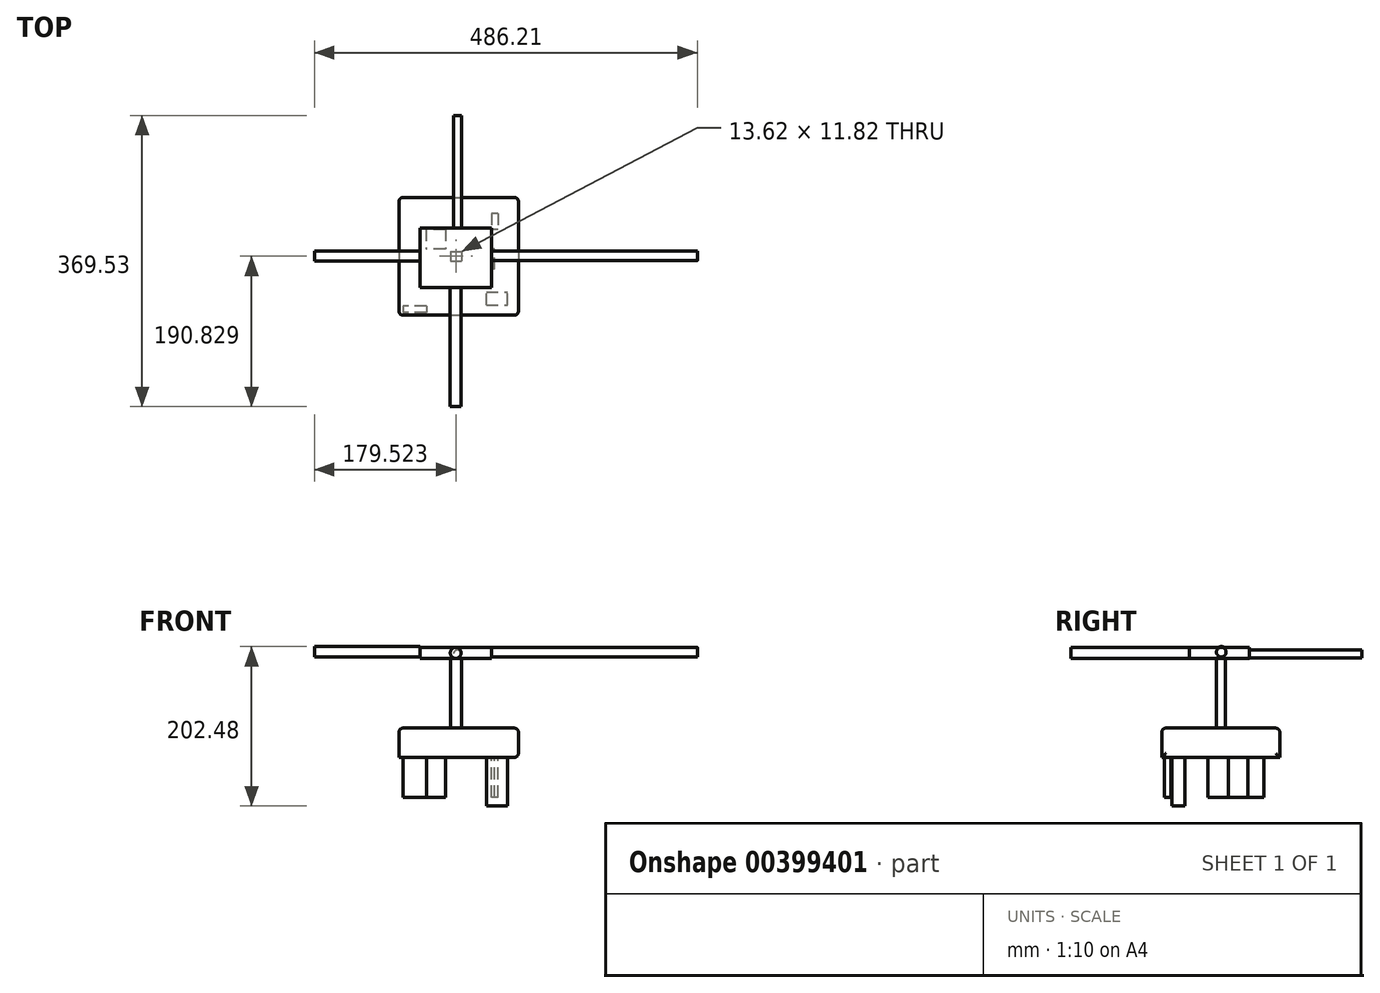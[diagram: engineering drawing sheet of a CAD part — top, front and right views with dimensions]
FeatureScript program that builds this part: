
annotation { "Feature Type Name" : "Feature", "Feature Type Description" : "" }
export const myFeature = defineFeature(function(context is Context, id is Id, definition is map)
    precondition{}
    {
        {
            var Q0;
            Q0=qCreatedBy(makeId("Top.planeOp"),FACE);
            var sketch = newSketch(context, id + "F0", { "sketchPlane" : qUnion([Q0])});
            skLineSegment(sketch, "E0.bottom", {"start": v(-74.23, 74.28) * mm, "end": v(77.35, 74.28) * mm});
            skLineSegment(sketch, "E0.top", {"start": v(-74.23, -75.35) * mm, "end": v(77.35, -75.35) * mm});
            skLineSegment(sketch, "E0.left", {"start": v(-74.23, 74.28) * mm, "end": v(-74.23, -75.35) * mm});
            skLineSegment(sketch, "E0.right", {"start": v(77.35, 74.28) * mm, "end": v(77.35, -75.35) * mm});
            skSolve(sketch);
        }
        {
            var Q0;
            Q0=makeQuery(id+"F0.imprint","IMPRINT",FACE,{"disambiguationData":[TD([[makeQuery(id+"F0.imprint","IMPRINT",EDGE,{"derivedFrom":sQuery(id+"F0.wireOp",EDGE,"E0.bottom")}),-1.0]])]});
            extrude(context, id + "F1", {"entities" : qUnion([Q0]), "depth" : 11.68 * mm});
        }
        {
            var Q0;
            Q0 = qSketchRegion(id + "FcFcLZ2dVXgPDsk_1", true);
            var Q1;
            Q1=makeQuery(id+"F1.opExtrude","CAP_FACE",FACE,{"disambiguationData":[OSD([sQuery(id+"F0.wireOp",EDGE,"E0.bottom"),sQuery(id+"F0.wireOp",EDGE,"E0.top"),sQuery(id+"F0.wireOp",EDGE,"E0.left"),sQuery(id+"F0.wireOp",EDGE,"E0.right")])],"isStart":true});
            extrude(context, id + "F2", {"entities" : qUnion([Q0, Q1]), "operationType" : NewBodyOperationType.ADD, "depth" : 25.4 * mm});
        }
        {
            var Q0;
            Q0=makeQuery(id+"F2.opExtrude","CAP_FACE",FACE,{"disambiguationData":[OSD([sQuery(id+"F0.wireOp",EDGE,"E0.bottom"),sQuery(id+"F0.wireOp",EDGE,"E0.top"),sQuery(id+"F0.wireOp",EDGE,"E0.left"),sQuery(id+"F0.wireOp",EDGE,"E0.right")])],"isStart":false});
            var sketch = newSketch(context, id + "F3", { "sketchPlane" : qUnion([Q0])});
            skLineSegment(sketch, "E1.bottom", {"start": v(51.45, -53.96) * mm, "end": v(43.06, -53.96) * mm});
            skLineSegment(sketch, "E1.top", {"start": v(51.45, -33.68) * mm, "end": v(43.06, -33.68) * mm});
            skLineSegment(sketch, "E1.left", {"start": v(51.45, -53.96) * mm, "end": v(51.45, -33.68) * mm});
            skLineSegment(sketch, "E1.right", {"start": v(43.06, -53.96) * mm, "end": v(43.06, -33.68) * mm});
            skPoint(sketch, "E2.firstSnap0", {"position": v(47.26, -33.68) * mm});
            skLineSegment(sketch, "E2.bottom", {"start": v(47.26, 16.82) * mm, "end": v(43.06, 16.82) * mm});
            skLineSegment(sketch, "E2.top", {"start": v(47.26, -8.95) * mm, "end": v(43.06, -8.95) * mm});
            skLineSegment(sketch, "E2.left", {"start": v(47.26, 16.82) * mm, "end": v(47.26, -8.95) * mm});
            skLineSegment(sketch, "E2.right", {"start": v(43.06, 16.82) * mm, "end": v(43.06, -8.95) * mm});
            skLineSegment(sketch, "E3.bottom", {"start": v(-39.26, 63.74) * mm, "end": v(-68.84, 63.74) * mm});
            skLineSegment(sketch, "E3.top", {"start": v(-39.26, 72.2) * mm, "end": v(-68.84, 72.2) * mm});
            skLineSegment(sketch, "E3.left", {"start": v(-39.26, 63.74) * mm, "end": v(-39.26, 72.2) * mm});
            skLineSegment(sketch, "E3.right", {"start": v(-68.84, 63.74) * mm, "end": v(-68.84, 72.2) * mm});
            skLineSegment(sketch, "E4.bottom", {"start": v(-15.31, -33.68) * mm, "end": v(-40.12, -33.68) * mm});
            skLineSegment(sketch, "E4.top", {"start": v(-15.31, -8.95) * mm, "end": v(-40.12, -8.95) * mm});
            skLineSegment(sketch, "E4.left", {"start": v(-15.31, -33.68) * mm, "end": v(-15.31, -8.95) * mm});
            skLineSegment(sketch, "E4.right", {"start": v(-40.12, -33.68) * mm, "end": v(-40.12, -8.95) * mm});
            skSolve(sketch);
        }
        {
            var Q0;
            Q0=makeQuery(id+"F1.opExtrude","CAP_FACE",FACE,{"disambiguationData":[OSD([sQuery(id+"F0.wireOp",EDGE,"E0.bottom"),sQuery(id+"F0.wireOp",EDGE,"E0.top"),sQuery(id+"F0.wireOp",EDGE,"E0.left"),sQuery(id+"F0.wireOp",EDGE,"E0.right")])],"isStart":false});
            var sketch = newSketch(context, id + "F4", { "sketchPlane" : qUnion([Q0])});
            skSolve(sketch);
        }
        {
            var Q0;
            Q0=makeQuery(id+"F3.imprint","IMPRINT",FACE,{"disambiguationData":[TD([[makeQuery(id+"F3.imprint","IMPRINT",EDGE,{"derivedFrom":sQuery(id+"F3.wireOp",EDGE,"E2.bottom")}),1.0]])]});
            var Q1;
            Q1=makeQuery(id+"F3.imprint","IMPRINT",FACE,{"disambiguationData":[TD([[makeQuery(id+"F3.imprint","IMPRINT",EDGE,{"derivedFrom":sQuery(id+"F3.wireOp",EDGE,"E4.bottom")}),-1.0]])]});
            var Q2;
            Q2=makeQuery(id+"F3.imprint","IMPRINT",FACE,{"disambiguationData":[TD([[makeQuery(id+"F3.imprint","IMPRINT",EDGE,{"derivedFrom":sQuery(id+"F3.wireOp",EDGE,"E1.bottom")}),-1.0]])]});
            var Q3;
            Q3=makeQuery(id+"F3.imprint","IMPRINT",FACE,{"disambiguationData":[TD([[makeQuery(id+"F3.imprint","IMPRINT",EDGE,{"derivedFrom":sQuery(id+"F3.wireOp",EDGE,"E3.bottom")}),-1.0]])]});
            extrude(context, id + "F5", {"entities" : qUnion([Q0, Q1, Q2, Q3]), "operationType" : NewBodyOperationType.ADD, "depth" : 25.4 * mm});
        }
        {
            var Q0;
            Q0=makeQuery(id+"F5.opExtrude","CAP_FACE",FACE,{"disambiguationData":[OSD([sQuery(id+"F3.wireOp",EDGE,"E3.bottom"),sQuery(id+"F3.wireOp",EDGE,"E3.top"),sQuery(id+"F3.wireOp",EDGE,"E3.left"),sQuery(id+"F3.wireOp",EDGE,"E3.right")])],"isStart":false});
            var Q1;
            Q1=makeQuery(id+"F5.opExtrude","CAP_FACE",FACE,{"disambiguationData":[OSD([sQuery(id+"F3.wireOp",EDGE,"E4.bottom"),sQuery(id+"F3.wireOp",EDGE,"E4.top"),sQuery(id+"F3.wireOp",EDGE,"E4.left"),sQuery(id+"F3.wireOp",EDGE,"E4.right")])],"isStart":false});
            var Q2;
            Q2=makeQuery(id+"F5.opExtrude","CAP_FACE",FACE,{"disambiguationData":[OSD([sQuery(id+"F3.wireOp",EDGE,"E2.bottom"),sQuery(id+"F3.wireOp",EDGE,"E2.top"),sQuery(id+"F3.wireOp",EDGE,"E2.left"),sQuery(id+"F3.wireOp",EDGE,"E2.right")])],"isStart":false});
            var Q3;
            Q3=makeQuery(id+"F5.opExtrude","CAP_FACE",FACE,{"disambiguationData":[OSD([sQuery(id+"F3.wireOp",EDGE,"E1.bottom"),sQuery(id+"F3.wireOp",EDGE,"E1.top"),sQuery(id+"F3.wireOp",EDGE,"E1.left"),sQuery(id+"F3.wireOp",EDGE,"E1.right")])],"isStart":false});
            extrude(context, id + "F6", {"entities" : qUnion([Q0, Q1, Q2, Q3]), "operationType" : NewBodyOperationType.ADD, "depth" : 25.4 * mm});
        }
        {
            var Q0;
            Q0=makeQuery(id+"F1.opExtrude","CAP_FACE",FACE,{"disambiguationData":[OSD([sQuery(id+"F0.wireOp",EDGE,"E0.bottom"),sQuery(id+"F0.wireOp",EDGE,"E0.top"),sQuery(id+"F0.wireOp",EDGE,"E0.left"),sQuery(id+"F0.wireOp",EDGE,"E0.right")])],"isStart":false});
            var sketch = newSketch(context, id + "F7", { "sketchPlane" : qUnion([Q0])});
            skSolve(sketch);
        }
        {
            var Q0;
            Q0=makeQuery(id+"F7.imprint","IMPRINT",FACE,{"disambiguationData":[TD([[makeQuery(id+"F7.imprint","IMPRINT",EDGE,{"derivedFrom":makeQuery(id+"F1.opExtrude","CAP_EDGE",EDGE,{"disambiguationData":[OSD([sQuery(id+"F0.wireOp",EDGE,"E0.bottom")])],"isStart":false})}),-1.0]])]});
            var sketch = newSketch(context, id + "F8", { "sketchPlane" : qUnion([Q0])});
            skLineSegment(sketch, "E5.bottom", {"start": v(-8.74, 5.5) * mm, "end": v(4.88, 5.5) * mm});
            skLineSegment(sketch, "E5.top", {"start": v(-8.74, -6.3) * mm, "end": v(4.88, -6.3) * mm});
            skLineSegment(sketch, "E5.left", {"start": v(-8.74, 5.5) * mm, "end": v(-8.74, -6.3) * mm});
            skLineSegment(sketch, "E5.right", {"start": v(4.88, 5.5) * mm, "end": v(4.88, -6.3) * mm});
            skSolve(sketch);
        }
        {
            var Q0;
            Q0=makeQuery(id+"F8.imprint","IMPRINT",FACE,{"disambiguationData":[TD([[makeQuery(id+"F8.imprint","IMPRINT",EDGE,{"derivedFrom":sQuery(id+"F8.wireOp",EDGE,"E5.bottom")}),-1.0]])]});
            extrude(context, id + "F9", {"entities" : qUnion([Q0]), "operationType" : NewBodyOperationType.ADD, "depth" : 88.65 * mm});
        }
        {
            var Q0;
            Q0=makeQuery(id+"F9.opExtrude","CAP_FACE",FACE,{"disambiguationData":[OSD([sQuery(id+"F8.wireOp",EDGE,"E5.bottom"),sQuery(id+"F8.wireOp",EDGE,"E5.top"),sQuery(id+"F8.wireOp",EDGE,"E5.left"),sQuery(id+"F8.wireOp",EDGE,"E5.right")])],"isStart":false});
            var sketch = newSketch(context, id + "F10", { "sketchPlane" : qUnion([Q0])});
            skLineSegment(sketch, "E6.bottom", {"start": v(-47.59, 35.55) * mm, "end": v(43.14, 35.55) * mm});
            skLineSegment(sketch, "E6.top", {"start": v(-47.59, -40.36) * mm, "end": v(43.14, -40.36) * mm});
            skLineSegment(sketch, "E6.left", {"start": v(-47.59, 35.55) * mm, "end": v(-47.59, -40.36) * mm});
            skLineSegment(sketch, "E6.right", {"start": v(43.14, 35.55) * mm, "end": v(43.14, -40.36) * mm});
            skSolve(sketch);
        }
        {
            var Q0;
            Q0 = qSketchRegion(id + "F10", true);
            extrude(context, id + "F11", {"entities" : qUnion([Q0]), "operationType" : NewBodyOperationType.ADD, "depth" : 13.97 * mm});
        }
        {
            var Q0;
            Q0=makeQuery(id+"F11.opExtrude","SWEPT_FACE",FACE,{"disambiguationData":[OSD([sQuery(id+"F10.wireOp",EDGE,"E6.top")])]});
            var sketch = newSketch(context, id + "F12", { "sketchPlane" : qUnion([Q0])});
            skCircle(sketch, "E7", {"center": v(-2.23, 107.31) * mm, "radius": 6.98 * mm});
            skPoint(sketch, "E7.centerSnap0", {"position": v(-2.23, 100.33) * mm});
            skPoint(sketch, "E7.centerSnap1", {"position": v(-47.59, 107.31) * mm});
            skSolve(sketch);
        }
        {
            var Q0;
            {var subQ0=sQuery(id+"F12.wireOp",EDGE,"E7");var subQ1=sQuery(id+"F10.wireOp",EDGE,"E6.top");var subQ2=makeQuery(id+"F12.imprint","INTERSECT",VERTEX,{"derivedFrom":[makeQuery(id+"F11.opExtrude","CAP_EDGE",EDGE,{"disambiguationData":[OSD([subQ1])],"isStart":true}),subQ0]});Q0=makeQuery(id+"F12.imprint","IMPRINT",FACE,{"disambiguationData":[TD([[makeQuery(id+"F12.imprint","IMPRINT",EDGE,{"disambiguationData":[TD([[subQ2,1.0]])],"derivedFrom":subQ0}),1.0]])]});}
            extrude(context, id + "F13", {"entities" : qUnion([Q0]), "operationType" : NewBodyOperationType.ADD, "depth" : 25.4 * mm});
        }
        {
            var Q0;
            Q0=makeQuery(id+"F13.opExtrude","CAP_FACE",FACE,{"disambiguationData":[OSD([sQuery(id+"F12.wireOp",EDGE,"E7")])],"isStart":false});
            extrude(context, id + "F14", {"entities" : qUnion([Q0]), "operationType" : NewBodyOperationType.ADD, "depth" : 125.48 * mm});
        }
        {
            var Q0;
            Q0=makeQuery(id+"F11.opExtrude","SWEPT_FACE",FACE,{"disambiguationData":[OSD([sQuery(id+"F10.wireOp",EDGE,"E6.right")])]});
            var sketch = newSketch(context, id + "F15", { "sketchPlane" : qUnion([Q0])});
            skCircle(sketch, "E8", {"center": v(0, 108.3) * mm, "radius": 6.1 * mm});
            skSolve(sketch);
        }
        {
            var Q0;
            {var subQ0=sQuery(id+"F15.wireOp",EDGE,"E8");var subQ1=makeQuery(id+"F11.opExtrude","CAP_EDGE",EDGE,{"disambiguationData":[OSD([sQuery(id+"F10.wireOp",EDGE,"E6.right")])],"isStart":false});var subQ2=makeQuery(id+"F15.imprint","INTERSECT",VERTEX,{"disambiguationData":[OD(0.0)],"derivedFrom":[subQ1,subQ0]});Q0=makeQuery(id+"F15.imprint","IMPRINT",FACE,{"disambiguationData":[TD([[makeQuery(id+"F15.imprint","IMPRINT",EDGE,{"disambiguationData":[TD([[subQ2,-1.0]])],"derivedFrom":subQ0}),1.0]])]});}
            var Q1;
            {var subQ0=sQuery(id+"F15.wireOp",EDGE,"E8");var subQ1=makeQuery(id+"F11.opExtrude","CAP_EDGE",EDGE,{"disambiguationData":[OSD([sQuery(id+"F10.wireOp",EDGE,"E6.right")])],"isStart":false});var subQ2=makeQuery(id+"F15.imprint","INTERSECT",VERTEX,{"disambiguationData":[OD(0.0)],"derivedFrom":[subQ1,subQ0]});Q1=makeQuery(id+"F15.imprint","IMPRINT",FACE,{"disambiguationData":[TD([[makeQuery(id+"F15.imprint","IMPRINT",EDGE,{"disambiguationData":[TD([[subQ2,1.0]])],"derivedFrom":subQ0}),1.0]])]});}
            extrude(context, id + "F16", {"entities" : qUnion([Q0, Q1]), "operationType" : NewBodyOperationType.ADD, "depth" : 25.4 * mm});
        }
        {
            var Q0;
            Q0=makeQuery(id+"F11.opExtrude","SWEPT_FACE",FACE,{"disambiguationData":[OSD([sQuery(id+"F10.wireOp",EDGE,"E6.bottom")])]});
            var sketch = newSketch(context, id + "F17", { "sketchPlane" : qUnion([Q0])});
            skCircle(sketch, "E9", {"center": v(0, 105.9) * mm, "radius": 4.97 * mm});
            skSolve(sketch);
        }
        {
            var Q0;
            Q0=makeQuery(id+"F17.imprint","IMPRINT",FACE,{"disambiguationData":[TD([[makeQuery(id+"F17.imprint","IMPRINT",EDGE,{"derivedFrom":sQuery(id+"F17.wireOp",EDGE,"E9")}),1.0]])]});
            extrude(context, id + "F18", {"entities" : qUnion([Q0]), "operationType" : NewBodyOperationType.ADD, "depth" : 117.35 * mm});
        }
        {
            var Q0;
            Q0=makeQuery(id+"F11.opExtrude","SWEPT_FACE",FACE,{"disambiguationData":[OSD([sQuery(id+"F10.wireOp",EDGE,"E6.left")])]});
            var sketch = newSketch(context, id + "F19", { "sketchPlane" : qUnion([Q0])});
            skCircle(sketch, "E10", {"center": v(0, 108.9) * mm, "radius": 6.46 * mm});
            skSolve(sketch);
        }
        {
            var Q0;
            {var subQ0=sQuery(id+"F19.wireOp",EDGE,"E10");var subQ1=makeQuery(id+"F11.opExtrude","CAP_EDGE",EDGE,{"disambiguationData":[OSD([sQuery(id+"F10.wireOp",EDGE,"E6.left")])],"isStart":false});var subQ2=makeQuery(id+"F19.imprint","INTERSECT",VERTEX,{"disambiguationData":[OD(0.0)],"derivedFrom":[subQ1,subQ0]});Q0=makeQuery(id+"F19.imprint","IMPRINT",FACE,{"disambiguationData":[TD([[makeQuery(id+"F19.imprint","IMPRINT",EDGE,{"disambiguationData":[TD([[subQ2,1.0]])],"derivedFrom":subQ0}),1.0]])]});}
            var Q1;
            {var subQ0=sQuery(id+"F19.wireOp",EDGE,"E10");var subQ1=makeQuery(id+"F11.opExtrude","CAP_EDGE",EDGE,{"disambiguationData":[OSD([sQuery(id+"F10.wireOp",EDGE,"E6.left")])],"isStart":false});var subQ2=makeQuery(id+"F19.imprint","INTERSECT",VERTEX,{"disambiguationData":[OD(0.0)],"derivedFrom":[subQ1,subQ0]});Q1=makeQuery(id+"F19.imprint","IMPRINT",FACE,{"disambiguationData":[TD([[makeQuery(id+"F19.imprint","IMPRINT",EDGE,{"disambiguationData":[TD([[subQ2,-1.0]])],"derivedFrom":subQ0}),1.0]])]});}
            extrude(context, id + "F20", {"entities" : qUnion([Q0, Q1]), "operationType" : NewBodyOperationType.ADD, "depth" : 87.38 * mm});
        }
        {
            var Q0;
            Q0=makeQuery(id+"F16.opExtrude","CAP_FACE",FACE,{"disambiguationData":[OSD([sQuery(id+"F15.wireOp",EDGE,"E8")])],"isStart":false});
            var sketch = newSketch(context, id + "F21", { "sketchPlane" : qUnion([Q0])});
            skSolve(sketch);
        }
        {
            var Q0;
            Q0=makeQuery(id+"F21.imprint","IMPRINT",FACE,{"disambiguationData":[TD([[makeQuery(id+"F21.imprint","IMPRINT",EDGE,{"derivedFrom":makeQuery(id+"F16.opExtrude","CAP_EDGE",EDGE,{"disambiguationData":[OSD([sQuery(id+"F15.wireOp",EDGE,"E8")])],"isStart":false})}),1.0]])]});
            extrude(context, id + "F22", {"entities" : qUnion([Q0]), "operationType" : NewBodyOperationType.ADD, "depth" : 25.4 * mm});
        }
        {
            var Q0;
            Q0=makeQuery(id+"F18.opExtrude","CAP_FACE",FACE,{"disambiguationData":[OSD([sQuery(id+"F17.wireOp",EDGE,"E9")])],"isStart":false});
            var Q1;
            Q1=makeQuery(id+"F14.opExtrude","CAP_FACE",FACE,{"disambiguationData":[OSD([sQuery(id+"F12.wireOp",EDGE,"E7")])],"isStart":false});
            extrude(context, id + "F23", {"entities" : qUnion([Q0, Q1]), "operationType" : NewBodyOperationType.ADD, "depth" : 25.4 * mm});
        }
        {
            var Q0;
            Q0=makeQuery(id+"F22.opExtrude","CAP_FACE",FACE,{"disambiguationData":[OSD([sQuery(id+"F15.wireOp",EDGE,"E8")])],"isStart":false});
            extrude(context, id + "F24", {"entities" : qUnion([Q0]), "operationType" : NewBodyOperationType.ADD, "depth" : 25.4 * mm});
        }
        {
            var Q0;
            Q0=makeQuery(id+"F1.opExtrude","CAP_EDGE",EDGE,{"disambiguationData":[OSD([sQuery(id+"F0.wireOp",EDGE,"E0.right")])],"isStart":false});
            var Q1;
            Q1=makeQuery(id+"F1.opExtrude","CAP_EDGE",EDGE,{"disambiguationData":[OSD([sQuery(id+"F0.wireOp",EDGE,"E0.top")])],"isStart":false});
            var Q2;
            Q2=makeQuery(id+"F1.opExtrude","CAP_EDGE",EDGE,{"disambiguationData":[OSD([sQuery(id+"F0.wireOp",EDGE,"E0.left")])],"isStart":false});
            var Q3;
            Q3=makeQuery(id+"F1.opExtrude","CAP_EDGE",EDGE,{"disambiguationData":[OSD([sQuery(id+"F0.wireOp",EDGE,"E0.bottom")])],"isStart":false});
            var Q4;
            {var subQ0=sQuery(id+"F0.wireOp",EDGE,"E0.right");Q4=makeQuery(id+"F2.boolean.opBoolean","MERGE",FACE,{"derivedFrom":[makeQuery(id+"F1.opExtrude","SWEPT_FACE",FACE,{"disambiguationData":[OSD([subQ0])]}),makeQuery(id+"F2.opExtrude","SWEPT_FACE",FACE,{"disambiguationData":[OSD([subQ0])]})]});}
            var Q5;
            {var subQ0=sQuery(id+"F0.wireOp",EDGE,"E0.right");var subQ1=sQuery(id+"F0.wireOp",EDGE,"E0.bottom");Q5=makeQuery(id+"F2.boolean.opBoolean","MERGE",EDGE,{"derivedFrom":[makeQuery(id+"F1.opExtrude","SWEPT_EDGE",EDGE,{"disambiguationData":[OSD([subQ1,subQ0])]}),makeQuery(id+"F2.opExtrude","SWEPT_EDGE",EDGE,{"disambiguationData":[OSD([subQ1,subQ0])]})]});}
            fillet(context, id + "F25", {"entities" : qUnion([Q0, Q1, Q2, Q3, Q4, Q5]), "radius" : 5.08 * mm, "tangentPropagation" : true, "allowEdgeOverflow" : false});
        }
        {
            var Q0;
            {var subQ0=sQuery(id+"F0.wireOp",EDGE,"E0.left");var subQ1=sQuery(id+"F0.wireOp",EDGE,"E0.top");Q0=makeQuery(id+"F2.boolean.opBoolean","MERGE",EDGE,{"derivedFrom":[makeQuery(id+"F1.opExtrude","SWEPT_EDGE",EDGE,{"disambiguationData":[OSD([subQ1,subQ0])]}),makeQuery(id+"F2.opExtrude","SWEPT_EDGE",EDGE,{"disambiguationData":[OSD([subQ1,subQ0])]})]});}
            var Q1;
            {var subQ0=sQuery(id+"F0.wireOp",EDGE,"E0.left");var subQ1=sQuery(id+"F0.wireOp",EDGE,"E0.bottom");Q1=makeQuery(id+"F2.boolean.opBoolean","MERGE",EDGE,{"derivedFrom":[makeQuery(id+"F1.opExtrude","SWEPT_EDGE",EDGE,{"disambiguationData":[OSD([subQ1,subQ0])]}),makeQuery(id+"F2.opExtrude","SWEPT_EDGE",EDGE,{"disambiguationData":[OSD([subQ1,subQ0])]})]});}
            fillet(context, id + "F26", {"entities" : qUnion([Q0, Q1]), "radius" : 5.08 * mm, "tangentPropagation" : true, "allowEdgeOverflow" : false});
        }
        {
            var Q0;
            Q0=makeQuery(id+"F2.opExtrude","CAP_FACE",FACE,{"disambiguationData":[OSD([sQuery(id+"F0.wireOp",EDGE,"E0.bottom"),sQuery(id+"F0.wireOp",EDGE,"E0.top"),sQuery(id+"F0.wireOp",EDGE,"E0.left"),sQuery(id+"F0.wireOp",EDGE,"E0.right")])],"isStart":false});
            var sketch = newSketch(context, id + "F27", { "sketchPlane" : qUnion([Q0])});
            skLineSegment(sketch, "E11.bottom", {"start": v(36.62, 62.56) * mm, "end": v(63.81, 62.56) * mm});
            skLineSegment(sketch, "E11.top", {"start": v(36.62, 46.04) * mm, "end": v(63.81, 46.04) * mm});
            skLineSegment(sketch, "E11.left", {"start": v(36.62, 62.56) * mm, "end": v(36.62, 46.04) * mm});
            skLineSegment(sketch, "E11.right", {"start": v(63.81, 62.56) * mm, "end": v(63.81, 46.04) * mm});
            skSolve(sketch);
        }
        {
            var Q0;
            Q0=makeQuery(id+"F27.imprint","IMPRINT",FACE,{"disambiguationData":[TD([[makeQuery(id+"F27.imprint","IMPRINT",EDGE,{"derivedFrom":sQuery(id+"F27.wireOp",EDGE,"E11.bottom")}),-1.0]])]});
            extrude(context, id + "F28", {"entities" : qUnion([Q0]), "operationType" : NewBodyOperationType.ADD, "depth" : 61.72 * mm});
        }
        {
            var Q0;
            Q0=makeQuery(id+"F24.opExtrude","CAP_FACE",FACE,{"disambiguationData":[OSD([sQuery(id+"F15.wireOp",EDGE,"E8")])],"isStart":false});
            extrude(context, id + "F29", {"entities" : qUnion([Q0]), "operationType" : NewBodyOperationType.ADD, "depth" : 25.4 * mm});
        }
        {
            var Q0;
            Q0=makeQuery(id+"F29.opExtrude","CAP_FACE",FACE,{"disambiguationData":[OSD([sQuery(id+"F15.wireOp",EDGE,"E8")])],"isStart":false});
            extrude(context, id + "F30", {"entities" : qUnion([Q0]), "operationType" : NewBodyOperationType.ADD, "depth" : 160.02 * mm});
        }
        {
            var Q0;
            Q0=makeQuery(id+"F20.opExtrude","CAP_FACE",FACE,{"disambiguationData":[OSD([sQuery(id+"F19.wireOp",EDGE,"E10")])],"isStart":false});
            extrude(context, id + "F31", {"entities" : qUnion([Q0]), "operationType" : NewBodyOperationType.ADD, "depth" : 46.48 * mm});
        }
    });
